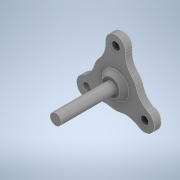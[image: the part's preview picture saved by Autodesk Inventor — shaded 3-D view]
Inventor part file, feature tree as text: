
AUTODESK INVENTOR PART (.ipt)
format: ipt  version: 2022 (Build 260153000, 153)  size: 160,768 bytes
history: mixed  units: in
note: dims shown in document units (in); Inventor stores cm internally (conversion verified against a paired STEP export)
features: extrude x1, sketch x1, chamfer x1, imported_body x1
ambient origin geometry x8: Origin, YZ Plane, XZ Plane, XY Plane, X Axis, Y Axis, Z Axis, Center Point
bodies: Solid1 (imported_parasolid)
feature tree (4):
  extrude  "Extrusion3"  [1 undecoded]
  sketch  "Sketch3"  dims[d4=0.9843in d5=0.0787in d6=0.0in d7=0.0in]
  chamfer  "Chamfer5"  [1 undecoded]
  imported_body  NMx_Import_Brep_tag  [imported B-rep: ~35 faces, bbox_mm=[31.788121, 26.496463, 31.0]]
note: 2 required parameter values undecoded (feature->parameter linkage not recoverable at this tier; creation-order binding heuristic only, values carry confidence <= 0.55)
